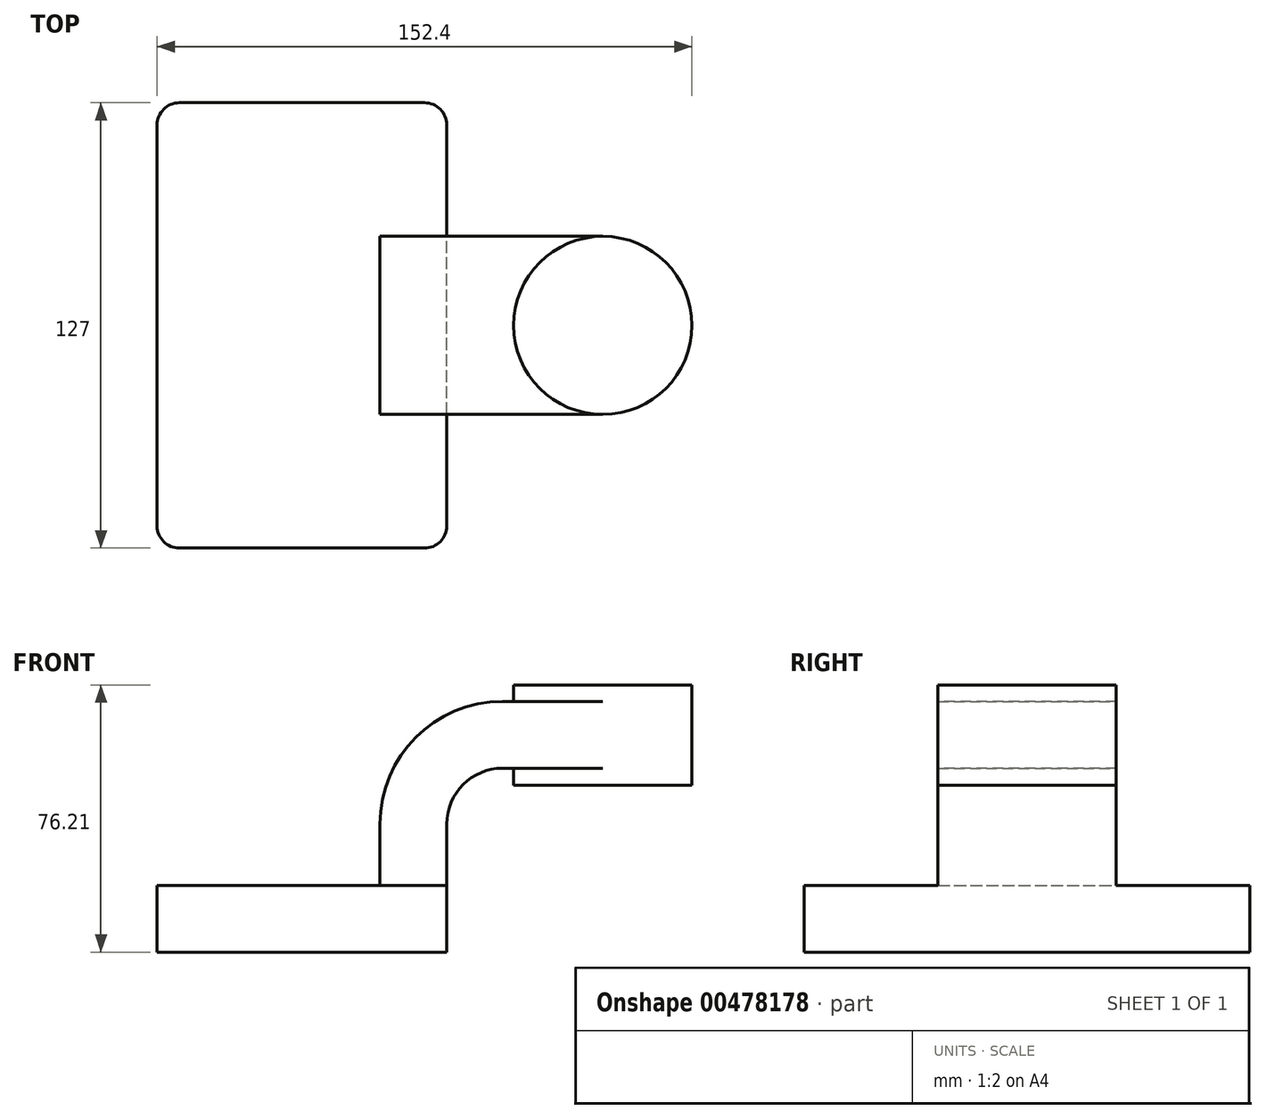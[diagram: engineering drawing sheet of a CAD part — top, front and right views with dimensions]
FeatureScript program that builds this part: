
annotation { "Feature Type Name" : "Feature", "Feature Type Description" : "" }
export const myFeature = defineFeature(function(context is Context, id is Id, definition is map)
    precondition{}
    {
        {
            var Q0;
            Q0=qCreatedBy(makeId("Front.planeOp"),FACE);
            var sketch = newSketch(context, id + "F0", { "sketchPlane" : qUnion([Q0])});
            skLineSegment(sketch, "E0.bottom", {"start": v(-41.27, -9.53) * mm, "end": v(41.28, -9.53) * mm});
            skLineSegment(sketch, "E0.top", {"start": v(-41.28, 9.53) * mm, "end": v(41.28, 9.53) * mm});
            skLineSegment(sketch, "E0.left", {"start": v(-41.28, -9.53) * mm, "end": v(-41.28, 9.53) * mm});
            skLineSegment(sketch, "E0.right", {"start": v(41.28, -9.53) * mm, "end": v(41.28, 9.53) * mm});
            skPoint(sketch, "E0.middle", {"position": v(0, 0) * mm});
            skLineSegment(sketch, "E1.bottom", {"start": v(60.32, 38.1) * mm, "end": v(111.12, 38.1) * mm});
            skLineSegment(sketch, "E1.top", {"start": v(60.32, 66.67) * mm, "end": v(111.12, 66.67) * mm});
            skLineSegment(sketch, "E1.left", {"start": v(60.32, 38.1) * mm, "end": v(60.32, 66.67) * mm});
            skLineSegment(sketch, "E1.right", {"start": v(111.12, 38.1) * mm, "end": v(111.12, 66.67) * mm});
            skPoint(sketch, "E1.middle", {"position": v(85.72, 52.39) * mm});
            skLineSegment(sketch, "E2", {"start": v(41.27, 9.53) * mm, "end": v(41.27, 27.01) * mm});
            skArc(sketch, "E3", {"start": v(41.27, 27.01) * mm, "mid": v(45.92, 38.24) * mm, "end": v(57.15, 42.89) * mm});
            skLineSegment(sketch, "E4", {"start": v(57.15, 42.89) * mm, "end": v(85.72, 42.89) * mm});
            skLineSegment(sketch, "E5.0", {"start": v(57.15, 61.94) * mm, "end": v(85.72, 61.94) * mm});
            skArc(sketch, "E5.1", {"start": v(22.23, 27.01) * mm, "mid": v(32.45, 51.7) * mm, "end": v(57.15, 61.94) * mm});
            skLineSegment(sketch, "E5.2", {"start": v(22.23, 9.53) * mm, "end": v(22.23, 27.01) * mm});
            skLineSegment(sketch, "E6", {"start": v(85.72, 66.67) * mm, "end": v(85.72, 42.89) * mm});
            skFitSpline(sketch, "E7", {"points": [v(57.15, 61.94) * mm, v(-41.28, 9.53) * mm], "startDerivative": vector(-110.56, 15.3) * mm, "endDerivative": vector(-62.8, -101.05) * mm});
            skLineSegment(sketch, "E8", {"start": v(85.72, 66.67) * mm, "end": v(85.72, 38.1) * mm});
            skSolve(sketch);
        }
        {
            var Q0;
            Q0=makeQuery(id+"F0.imprint","IMPRINT",FACE,{"disambiguationData":[TD([[makeQuery(id+"F0.imprint","IMPRINT",EDGE,{"derivedFrom":sQuery(id+"F0.wireOp",EDGE,"E0.bottom")}),1.0]])]});
            extrude(context, id + "F1", {"entities" : qUnion([Q0]), "endBound" : BoundingType.SYMMETRIC, "depth" : 127 * mm});
        }
        {
            var Q0;
            {var subQ1=sQuery(id+"F0.wireOp",EDGE,"E2");Q0=makeQuery(id+"F0.imprint","IMPRINT",FACE,{"disambiguationData":[TD([[makeQuery(id+"F0.imprint","IMPRINT",EDGE,{"derivedFrom":subQ1}),1.0]])]});}
            var Q1;
            {var subQ0=sQuery(id+"F0.wireOp",EDGE,"E4");var subQ1=sQuery(id+"F0.wireOp",EDGE,"E1.left");var subQ2=makeQuery(id+"F0.imprint","INTERSECT",VERTEX,{"derivedFrom":[subQ1,subQ0]});Q1=makeQuery(id+"F0.imprint","IMPRINT",FACE,{"disambiguationData":[TD([[makeQuery(id+"F0.imprint","IMPRINT",EDGE,{"disambiguationData":[TD([[subQ2,-1.0]])],"derivedFrom":subQ1}),-1.0]])]});}
            extrude(context, id + "F2", {"entities" : qUnion([Q0, Q1]), "operationType" : NewBodyOperationType.ADD, "endBound" : BoundingType.SYMMETRIC, "depth" : 50.8 * mm});
        }
        {
            var Q0;
            Q0=makeQuery(id+"F0.imprint","IMPRINT",FACE,{"disambiguationData":[TD([[makeQuery(id+"F0.imprint","IMPRINT",EDGE,{"derivedFrom":sQuery(id+"F0.wireOp",EDGE,"E5.1")}),1.0]])]});
            extrude(context, id + "F3", {"entities" : qUnion([Q0]), "operationType" : NewBodyOperationType.ADD, "endBound" : BoundingType.SYMMETRIC, "depth" : 12.7 * mm});
        }
        {
            var Q0;
            {var subQ4=sQuery(id+"F0.wireOp",EDGE,"E1.right");Q0=makeQuery(id+"F0.imprint","IMPRINT",FACE,{"disambiguationData":[TD([[makeQuery(id+"F0.imprint","IMPRINT",EDGE,{"derivedFrom":subQ4}),1.0]])]});}
            var Q1;
            Q1=sQuery(id+"F0.wireOp",EDGE,"E8");
            revolve(context, id + "F4", {"operationType" : NewBodyOperationType.ADD, "entities" : qUnion([Q0]), "axis" : qUnion([Q1]), "revolveType" : RevolveType.FULL});
        }
        {
            var Q0;
            Q0=makeQuery(id+"F1.opExtrude","CAP_EDGE",EDGE,{"disambiguationData":[OSD([sQuery(id+"F0.wireOp",EDGE,"E0.right")])],"isStart":false});
            var Q1;
            Q1=makeQuery(id+"F1.opExtrude","CAP_EDGE",EDGE,{"disambiguationData":[OSD([sQuery(id+"F0.wireOp",EDGE,"E0.left")])],"isStart":false});
            var Q2;
            Q2=makeQuery(id+"F1.opExtrude","CAP_EDGE",EDGE,{"disambiguationData":[OSD([sQuery(id+"F0.wireOp",EDGE,"E0.right")])],"isStart":true});
            var Q3;
            Q3=makeQuery(id+"F1.opExtrude","CAP_EDGE",EDGE,{"disambiguationData":[OSD([sQuery(id+"F0.wireOp",EDGE,"E0.left")])],"isStart":true});
            fillet(context, id + "F5", {"entities" : qUnion([Q0, Q1, Q2, Q3]), "radius" : 6.35 * mm, "tangentPropagation" : true, "allowEdgeOverflow" : false});
        }
    });
